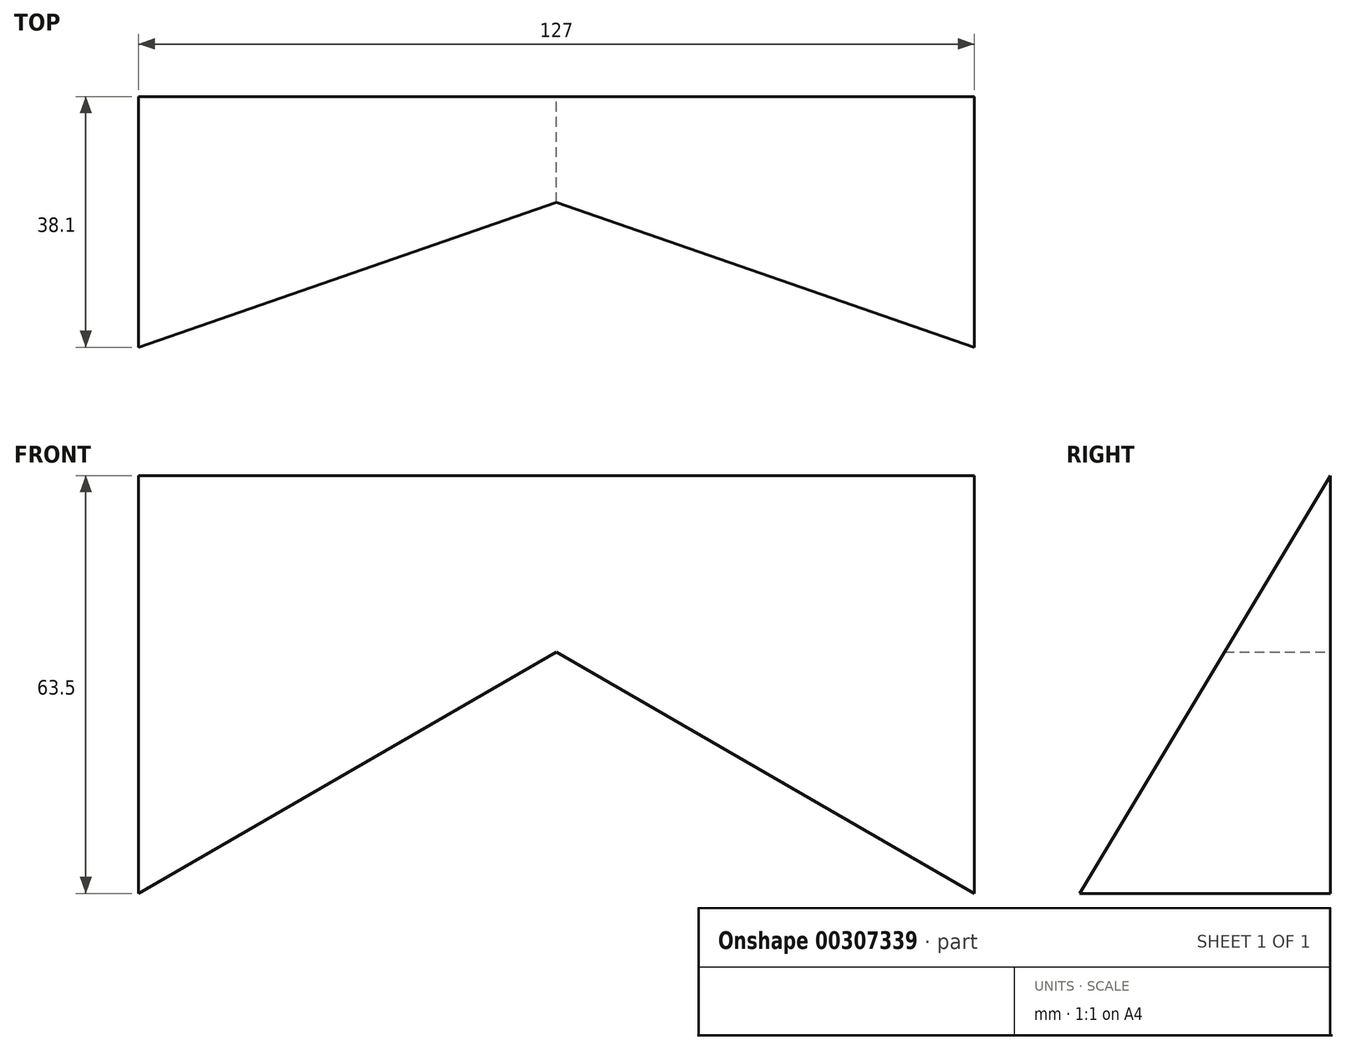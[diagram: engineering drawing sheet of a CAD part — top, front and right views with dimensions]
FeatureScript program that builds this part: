
annotation { "Feature Type Name" : "Feature", "Feature Type Description" : "" }
export const myFeature = defineFeature(function(context is Context, id is Id, definition is map)
    precondition{}
    {
        {
            var Q0;
            Q0=qCreatedBy(makeId("Front.planeOp"),FACE);
            var sketch = newSketch(context, id + "F0", { "sketchPlane" : qUnion([Q0])});
            skLineSegment(sketch, "E0", {"start": v(-63.5, 38.93) * mm, "end": v(63.5, 38.93) * mm});
            skLineSegment(sketch, "E1", {"start": v(63.5, 38.93) * mm, "end": v(63.5, -24.57) * mm});
            skLineSegment(sketch, "E2", {"start": v(63.5, -24.57) * mm, "end": v(0, 12.09) * mm});
            skLineSegment(sketch, "E3", {"start": v(0, 12.09) * mm, "end": v(-63.5, -24.57) * mm});
            skLineSegment(sketch, "E4", {"start": v(-63.5, -24.57) * mm, "end": v(-63.5, 38.93) * mm});
            skSolve(sketch);
        }
        {
            var Q0;
            Q0 = qSketchRegion(id + "F0", true);
            extrude(context, id + "F1", {"entities" : qUnion([Q0]), "depth" : 38.1 * mm});
        }
        {
            var Q0;
            Q0=makeQuery(id+"F1.opExtrude","SWEPT_FACE",FACE,{"disambiguationData":[OSD([sQuery(id+"F0.wireOp",EDGE,"E1")])]});
            var sketch = newSketch(context, id + "F2", { "sketchPlane" : qUnion([Q0])});
            skLineSegment(sketch, "E5", {"start": v(-38.1, -24.57) * mm, "end": v(0, 38.93) * mm});
            skSolve(sketch);
        }
        {
            var Q0;
            Q0=makeQuery(id+"F2.imprint","IMPRINT",FACE,{"disambiguationData":[TD([[makeQuery(id+"F2.imprint","IMPRINT",EDGE,{"derivedFrom":sQuery(id+"F2.wireOp",EDGE,"E5")}),1.0]])]});
            extrude(context, id + "F3", {"entities" : qUnion([Q0]), "operationType" : NewBodyOperationType.REMOVE, "oppositeDirection" : true, "depth" : 127 * mm});
        }
    });
